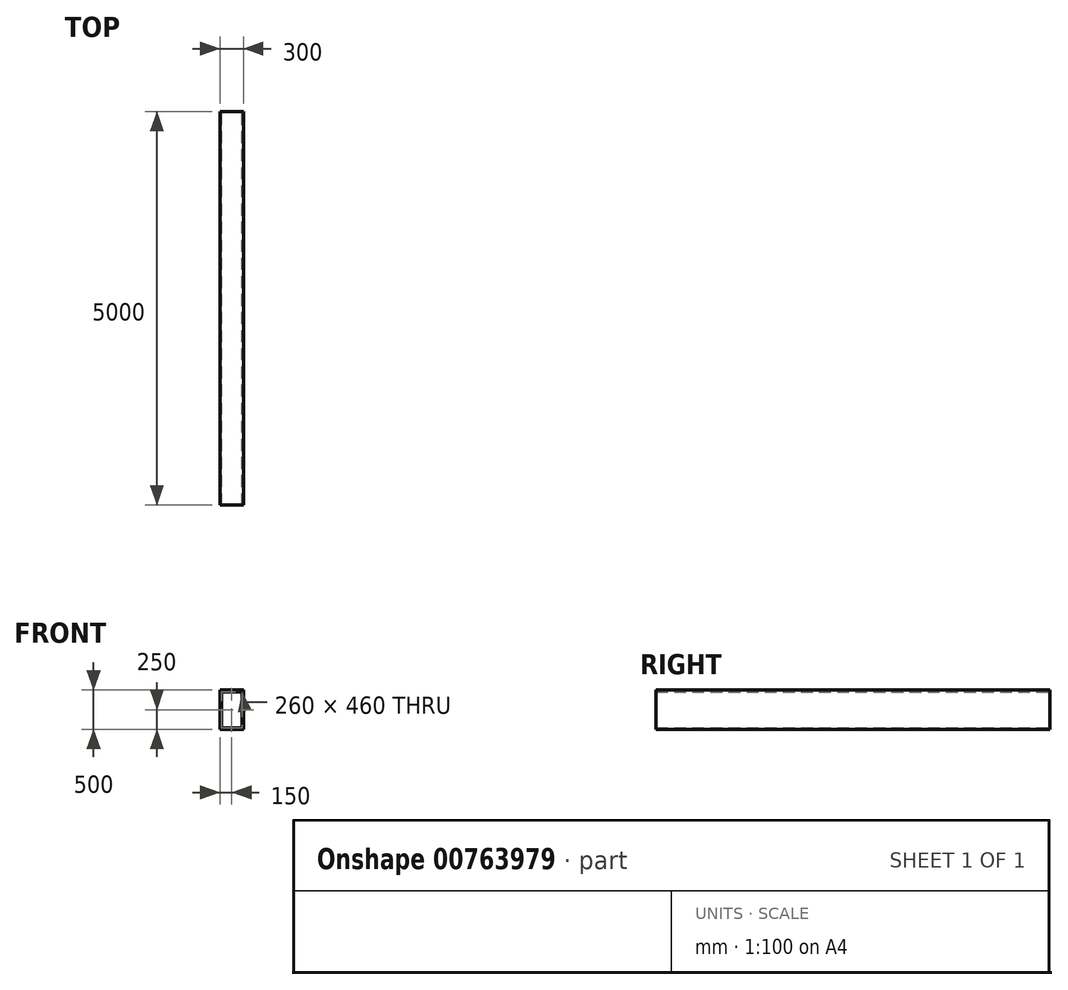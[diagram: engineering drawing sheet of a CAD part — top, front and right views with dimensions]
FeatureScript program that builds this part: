
annotation { "Feature Type Name" : "Feature", "Feature Type Description" : "" }
export const myFeature = defineFeature(function(context is Context, id is Id, definition is map)
    precondition{}
    {
        {
            var Q0;
            Q0=qCreatedBy(makeId("Front.planeOp"),FACE);
            var sketch = newSketch(context, id + "F0", { "sketchPlane" : qUnion([Q0])});
            skLineSegment(sketch, "E0.bottom", {"start": v(-150, 250) * mm, "end": v(150, 250) * mm});
            skLineSegment(sketch, "E0.top", {"start": v(-150, -250) * mm, "end": v(150, -250) * mm});
            skLineSegment(sketch, "E0.left", {"start": v(-150, 250) * mm, "end": v(-150, -250) * mm});
            skLineSegment(sketch, "E0.right", {"start": v(150, 250) * mm, "end": v(150, -250) * mm});
            skLineSegment(sketch, "E1.bottom", {"start": v(-130, 230) * mm, "end": v(130, 230) * mm});
            skLineSegment(sketch, "E1.top", {"start": v(-130, -230) * mm, "end": v(130, -230) * mm});
            skLineSegment(sketch, "E1.left", {"start": v(-130, 230) * mm, "end": v(-130, -230) * mm});
            skLineSegment(sketch, "E1.right", {"start": v(130, 230) * mm, "end": v(130, -230) * mm});
            skSolve(sketch);
        }
        {
            var Q0;
            Q0=makeQuery(id+"F0.imprint","IMPRINT",FACE,{"disambiguationData":[TD([[makeQuery(id+"F0.imprint","IMPRINT",EDGE,{"derivedFrom":sQuery(id+"F0.wireOp",EDGE,"E0.bottom")}),-1.0]])]});
            extrude(context, id + "F1", {"entities" : qUnion([Q0]), "endBound" : BoundingType.SYMMETRIC, "depth" : 5000 * mm, "offsetDistance" : 25 * mm});
        }
    });
